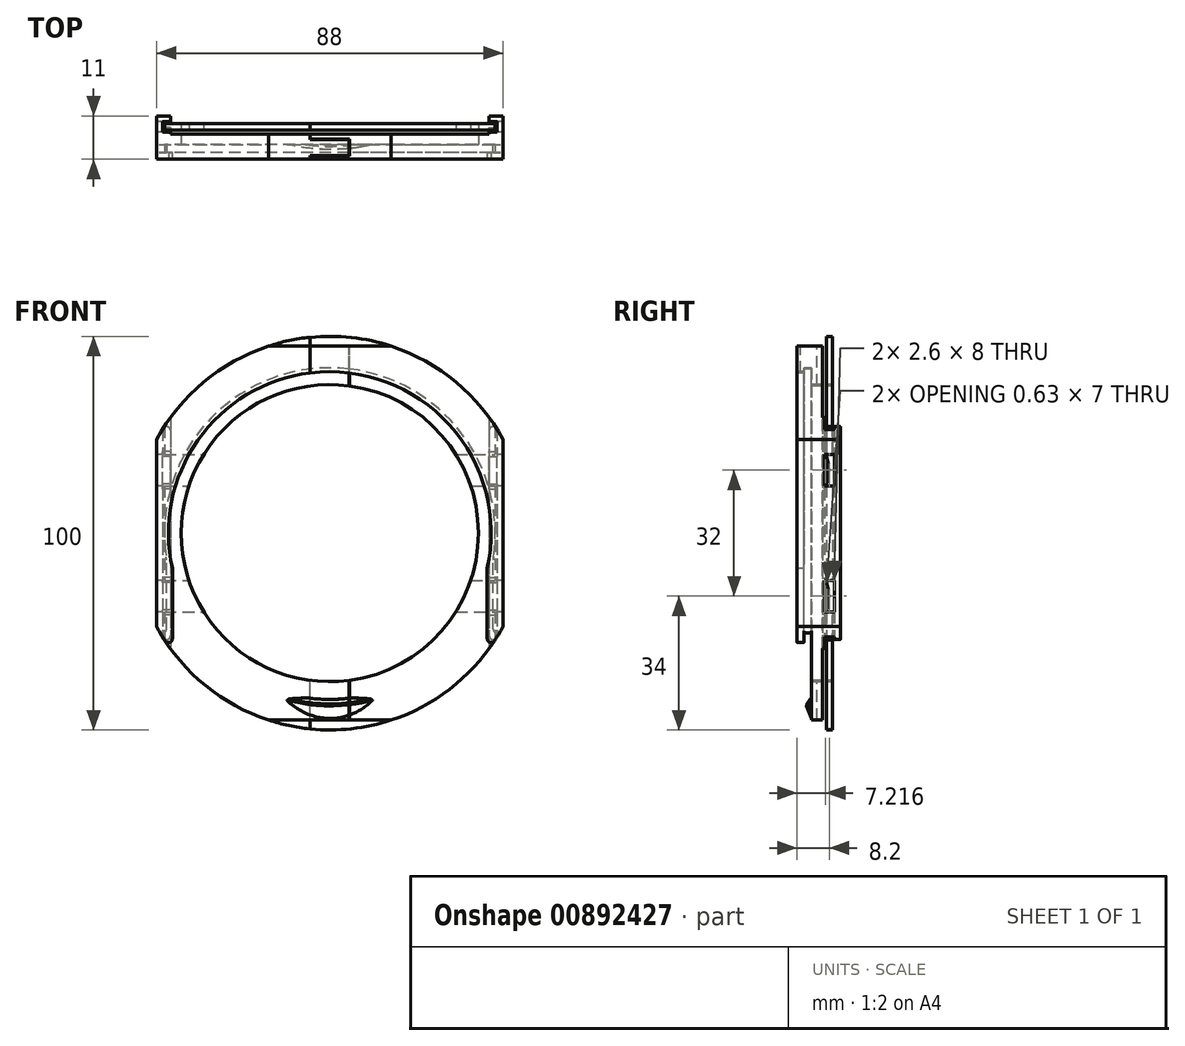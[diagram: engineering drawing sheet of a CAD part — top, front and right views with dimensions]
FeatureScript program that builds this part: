
annotation { "Feature Type Name" : "Feature", "Feature Type Description" : "" }
export const myFeature = defineFeature(function(context is Context, id is Id, definition is map)
    precondition{}
    {
        {
            var Q0;
            Q0=qCreatedBy(makeId("Front.planeOp"),FACE);
            var sketch = newSketch(context, id + "F0", { "sketchPlane" : qUnion([Q0])});
            skLineSegment(sketch, "E0.bottom", {"start": v(42, 50) * mm, "end": v(-42, 50) * mm});
            skLineSegment(sketch, "E0.top", {"start": v(42, -50) * mm, "end": v(-42, -50) * mm});
            skLineSegment(sketch, "E0.left", {"start": v(42, 50) * mm, "end": v(42, -50) * mm});
            skLineSegment(sketch, "E0.right", {"start": v(-42, 50) * mm, "end": v(-42, -50) * mm});
            skPoint(sketch, "E0.middle", {"position": v(0, 0) * mm});
            skSolve(sketch);
        }
        {
            var Q0;
            Q0=makeQuery(id+"F0.imprint","IMPRINT",FACE,{"disambiguationData":[TD([[makeQuery(id+"F0.imprint","IMPRINT",EDGE,{"derivedFrom":sQuery(id+"F0.wireOp",EDGE,"E0.bottom")}),1.0]])]});
            extrude(context, id + "F1", {"entities" : qUnion([Q0]), "depth" : .8 * mm, "offsetDistance" : 25 * mm, "hasSecondDirection" : true, "secondDirectionOppositeDirection" : true, "secondDirectionDepth" : .8 * mm});
        }
        {
            var Q0;
            Q0=qCreatedBy(makeId("Top.planeOp"),FACE);
            var sketch = newSketch(context, id + "F2", { "sketchPlane" : qUnion([Q0])});
            skLineSegment(sketch, "E1.0", {"start": v(42, 0.8) * mm, "end": v(-42, 0.8) * mm, "construction": true});
            skLineSegment(sketch, "E2.0", {"start": v(-42, -0.8) * mm, "end": v(-42, 0.8) * mm, "construction": true});
            skLineSegment(sketch, "E3.0", {"start": v(42, -0.8) * mm, "end": v(-42, -0.8) * mm, "construction": true});
            skLineSegment(sketch, "E4.0", {"start": v(42, -0.8) * mm, "end": v(42, 0.8) * mm, "construction": true});
            skLineSegment(sketch, "E5", {"start": v(-42.5, 1.3) * mm, "end": v(-42.5, -1.3) * mm});
            skLineSegment(sketch, "E6", {"start": v(-42.5, 1.3) * mm, "end": v(-40.5, 1.3) * mm});
            skLineSegment(sketch, "E7.MirrorCS", {"start": v(42.5, 1.3) * mm, "end": v(42.5, -1.3) * mm});
            skLineSegment(sketch, "E8.MirrorCS", {"start": v(42.5, 1.3) * mm, "end": v(40.5, 1.3) * mm});
            skLineSegment(sketch, "E9", {"start": v(-40.5, 1.3) * mm, "end": v(-40.5, 2.8) * mm});
            skLineSegment(sketch, "E10", {"start": v(-40.5, 2.8) * mm, "end": v(-44, 2.8) * mm});
            skLineSegment(sketch, "E11", {"start": v(-44, 2.8) * mm, "end": v(-44, -8.2) * mm});
            skLineSegment(sketch, "E12.MirrorCS", {"start": v(40.5, 1.3) * mm, "end": v(40.5, 2.8) * mm});
            skLineSegment(sketch, "E13.MirrorCS", {"start": v(40.5, 2.8) * mm, "end": v(44, 2.8) * mm});
            skLineSegment(sketch, "E14.MirrorCS", {"start": v(44, 2.8) * mm, "end": v(44, -8.2) * mm});
            skLineSegment(sketch, "E15", {"start": v(-44, -8.2) * mm, "end": v(44, -8.2) * mm});
            skLineSegment(sketch, "E16", {"start": v(-42.5, -1.3) * mm, "end": v(-40.5, -1.3) * mm});
            skLineSegment(sketch, "E17", {"start": v(-40.5, -1.3) * mm, "end": v(-40.5, -1.8) * mm});
            skLineSegment(sketch, "E18.MirrorCS", {"start": v(42.5, -1.3) * mm, "end": v(40.5, -1.3) * mm});
            skLineSegment(sketch, "E19.MirrorCS", {"start": v(40.5, -1.3) * mm, "end": v(40.5, -1.8) * mm});
            skLineSegment(sketch, "E20", {"start": v(40.5, -1.8) * mm, "end": v(-40.5, -1.8) * mm});
            skSolve(sketch);
        }
        {
            var Q0;
            Q0 = qSketchRegion(id + "F2", true);
            extrude(context, id + "F3", {"entities" : qUnion([Q0]), "endBound" : BoundingType.SYMMETRIC, "depth" : 95 * mm, "offsetDistance" : 25 * mm});
        }
        {
            var Q0;
            Q0=qCreatedBy(makeId("Right.planeOp"),FACE);
            var sketch = newSketch(context, id + "F4", { "sketchPlane" : qUnion([Q0])});
            skLineSegment(sketch, "E21.top", {"start": v(3, 37.75) * mm, "end": v(-4.5, 37.75) * mm});
            skLineSegment(sketch, "E22", {"start": v(-4.5, 37.75) * mm, "end": v(-4.5, 42) * mm});
            skLineSegment(sketch, "E23", {"start": v(-4.5, 42) * mm, "end": v(-6.5, 42) * mm});
            skLineSegment(sketch, "E24", {"start": v(-6.5, 42) * mm, "end": v(-6.5, 41) * mm});
            skLineSegment(sketch, "E25", {"start": v(-6.5, 41) * mm, "end": v(-8.5, 41) * mm});
            skLineSegment(sketch, "E26", {"start": v(-8.5, 41) * mm, "end": v(-8.5, 0) * mm});
            skLineSegment(sketch, "E27", {"start": v(3, 37.75) * mm, "end": v(3, 0) * mm});
            skLineSegment(sketch, "E28", {"start": v(3, 0) * mm, "end": v(-8.5, 0) * mm});
            skSolve(sketch);
        }
        {
            var Q0;
            Q0 = qSketchRegion(id + "F4", true);
            var Q1;
            Q1=sQuery(id+"F4.wireOp",EDGE,"E28");
            revolve(context, id + "F5", {"operationType" : NewBodyOperationType.REMOVE, "surfaceOperationType" : NewSurfaceOperationType.NEW, "entities" : qUnion([Q0]), "axis" : qUnion([Q1]), "revolveType" : RevolveType.FULL, "oppositeDirection" : true});
        }
        {
            var Q0;
            Q0=makeQuery(id+"F3.opExtrude","SWEPT_FACE",FACE,{"disambiguationData":[OSD([sQuery(id+"F2.wireOp",EDGE,"E15")])]});
            var sketch = newSketch(context, id + "F6", { "sketchPlane" : qUnion([Q0])});
            skLineSegment(sketch, "E29.0.0", {"start": v(-44, -47.5) * mm, "end": v(44, -47.5) * mm, "construction": true});
            skLineSegment(sketch, "E29.0.1", {"start": v(44, -47.5) * mm, "end": v(44, 47.5) * mm, "construction": true});
            skLineSegment(sketch, "E29.0.2", {"start": v(44, 47.5) * mm, "end": v(-44, 47.5) * mm, "construction": true});
            skLineSegment(sketch, "E29.0.3", {"start": v(-44, 47.5) * mm, "end": v(-44, -47.5) * mm, "construction": true});
            skLineSegment(sketch, "E30", {"start": v(-40, -9) * mm, "end": v(-40, -47.5) * mm});
            skLineSegment(sketch, "E31", {"start": v(40, -9) * mm, "end": v(40, -47.5) * mm});
            skArc(sketch, "E32", {"start": v(-40, -9) * mm, "mid": v(0, -41) * mm, "end": v(40, -9) * mm});
            skLineSegment(sketch, "E33", {"start": v(-40, -47.5) * mm, "end": v(40, -47.5) * mm});
            skSolve(sketch);
        }
        {
            var Q0;
            Q0 = qSketchRegion(id + "F6", true);
            var Q1;
            Q1=makeQuery(id+"F5.boolean.opBoolean","COPY",FACE,{"derivedFrom":makeQuery(id+"F5.opRevolve","SWEPT_FACE",FACE,{"disambiguationData":[OSD([sQuery(id+"F4.wireOp",EDGE,"E22")])]})});
            extrude(context, id + "F7", {"entities" : qUnion([Q0]), "operationType" : NewBodyOperationType.REMOVE, "endBound" : BoundingType.UP_TO_SURFACE, "oppositeDirection" : true, "depth" : 25 * mm, "endBoundEntityFace" : qUnion([Q1]), "offsetDistance" : 25 * mm});
        }
        {
            var Q0;
            Q0=qCreatedBy(makeId("Front.planeOp"),FACE);
            var sketch = newSketch(context, id + "F8", { "sketchPlane" : qUnion([Q0])});
            skCircle(sketch, "E34", {"center": v(0, 0) * mm, "radius": 50 * mm});
            skCircle(sketch, "E35", {"center": v(0, 0) * mm, "radius": 70 * mm});
            skSolve(sketch);
        }
        {
            var Q0;
            Q0 = qSketchRegion(id + "F8", true);
            extrude(context, id + "F9", {"entities" : qUnion([Q0]), "operationType" : NewBodyOperationType.REMOVE, "endBound" : BoundingType.SYMMETRIC, "oppositeDirection" : true, "depth" : 500 * mm, "offsetDistance" : 25 * mm});
        }
        {
            var Q0;
            Q0=qCreatedBy(makeId("Top.planeOp"),FACE);
            var sketch = newSketch(context, id + "F10", { "sketchPlane" : qUnion([Q0])});
            skLineSegment(sketch, "E36", {"start": v(-42, -4.5) * mm, "end": v(-42, -3.5) * mm, "construction": true});
            skLineSegment(sketch, "E37", {"start": v(42, -4.5) * mm, "end": v(42, -6.5) * mm, "construction": true});
            skLineSegment(sketch, "E38.bottom", {"start": v(-41.5, -4.5) * mm, "end": v(41.5, -4.5) * mm});
            skLineSegment(sketch, "E38.left", {"start": v(-41.5, -6.5) * mm, "end": v(-41.5, -4.5) * mm});
            skLineSegment(sketch, "E38.right", {"start": v(41.5, -6.5) * mm, "end": v(41.5, -4.5) * mm});
            skLineSegment(sketch, "E39.0.0", {"start": v(-15.61, -4.5) * mm, "end": v(15.61, -4.5) * mm});
            skLineSegment(sketch, "E39.0.1", {"start": v(15.61, -4.5) * mm, "end": v(40, -4.5) * mm});
            skLineSegment(sketch, "E39.0.3", {"start": v(42, -4.5) * mm, "end": v(-42, -4.5) * mm, "construction": true});
            skLineSegment(sketch, "E39.0.5", {"start": v(-40, -4.5) * mm, "end": v(-15.61, -4.5) * mm});
            skLineSegment(sketch, "E40.0", {"start": v(41, -6.5) * mm, "end": v(-41, -6.5) * mm, "construction": true});
            skLineSegment(sketch, "E41", {"start": v(-41.5, -6.5) * mm, "end": v(41.5, -6.5) * mm});
            skSolve(sketch);
        }
        {
            var Q0;
            Q0 = qSketchRegion(id + "F10", true);
            extrude(context, id + "F11", {"entities" : qUnion([Q0]), "operationType" : NewBodyOperationType.REMOVE, "oppositeDirection" : true, "depth" : 50 * mm, "offsetDistance" : 25 * mm});
        }
        {
            var Q0;
            Q0=makeQuery(id+"F11.boolean.opBoolean","INTERSECT",EDGE,{"derivedFrom":[makeQuery(id+"F5.boolean.opBoolean","COPY",FACE,{"derivedFrom":makeQuery(id+"F5.opRevolve","SWEPT_FACE",FACE,{"disambiguationData":[OSD([sQuery(id+"F4.wireOp",EDGE,"E23")])]})}),makeQuery(id+"F11.opExtrude","SWEPT_FACE",FACE,{"disambiguationData":[OSD([sQuery(id+"F10.wireOp",EDGE,"E38.right")])]})]});
            var Q1;
            Q1=makeQuery(id+"F11.boolean.opBoolean","INTERSECT",EDGE,{"derivedFrom":[makeQuery(id+"F5.boolean.opBoolean","COPY",FACE,{"derivedFrom":makeQuery(id+"F5.opRevolve","SWEPT_FACE",FACE,{"disambiguationData":[OSD([sQuery(id+"F4.wireOp",EDGE,"E23")])]})}),makeQuery(id+"F11.opExtrude","SWEPT_FACE",FACE,{"disambiguationData":[OSD([sQuery(id+"F10.wireOp",EDGE,"E38.left")])]})]});
            fillet(context, id + "F12", {"entities" : qUnion([Q0, Q1]), "radius" : 5 * mm, "tangentPropagation" : true, "allowEdgeOverflow" : false});
        }
        {
            var Q0;
            {var subQ0=sQuery(id+"F2.wireOp",EDGE,"E16");var subQ1=sQuery(id+"F2.wireOp",EDGE,"E11");var subQ2=sQuery(id+"F2.wireOp",EDGE,"E10");var subQ3=sQuery(id+"F2.wireOp",EDGE,"E5");var subQ4=sQuery(id+"F2.wireOp",EDGE,"E15");var subQ5=sQuery(id+"F2.wireOp",EDGE,"E20");var subQ6=sQuery(id+"F2.wireOp",EDGE,"E17");var subQ7=sQuery(id+"F2.wireOp",EDGE,"E9");var subQ8=sQuery(id+"F2.wireOp",EDGE,"E6");Q0=makeQuery(id+"F11.boolean.opBoolean","INTERSECT",EDGE,{"derivedFrom":[makeQuery(id+"F9.boolean.opBoolean","COPY",FACE,{"disambiguationData":[TD([makeQuery(id+"F3.opExtrude","SWEPT_FACE",FACE,{"disambiguationData":[OSD([subQ3])]}),makeQuery(id+"F3.opExtrude","CAP_FACE",FACE,{"disambiguationData":[OSD([subQ3,subQ8,sQuery(id+"F2.wireOp",EDGE,"E7.MirrorCS"),sQuery(id+"F2.wireOp",EDGE,"E8.MirrorCS"),subQ7,subQ2,subQ1,sQuery(id+"F2.wireOp",EDGE,"E12.MirrorCS"),sQuery(id+"F2.wireOp",EDGE,"E13.MirrorCS"),sQuery(id+"F2.wireOp",EDGE,"E14.MirrorCS"),subQ4,subQ0,subQ6,sQuery(id+"F2.wireOp",EDGE,"E18.MirrorCS"),sQuery(id+"F2.wireOp",EDGE,"E19.MirrorCS"),subQ5])],"isStart":true}),makeQuery(id+"F3.opExtrude","SWEPT_FACE",FACE,{"disambiguationData":[OSD([subQ8])]}),makeQuery(id+"F3.opExtrude","SWEPT_FACE",FACE,{"disambiguationData":[OSD([subQ7])]}),makeQuery(id+"F3.opExtrude","SWEPT_FACE",FACE,{"disambiguationData":[OSD([subQ2])]}),makeQuery(id+"F3.opExtrude","SWEPT_FACE",FACE,{"disambiguationData":[OSD([subQ1])]}),makeQuery(id+"F3.opExtrude","SWEPT_FACE",FACE,{"disambiguationData":[OSD([subQ4])]}),makeQuery(id+"F3.opExtrude","SWEPT_FACE",FACE,{"disambiguationData":[OSD([subQ0])]}),makeQuery(id+"F3.opExtrude","SWEPT_FACE",FACE,{"disambiguationData":[OSD([subQ6])]}),makeQuery(id+"F3.opExtrude","SWEPT_FACE",FACE,{"disambiguationData":[OSD([subQ5])]}),makeQuery(id+"F5.boolean.opBoolean","COPY",FACE,{"derivedFrom":makeQuery(id+"F5.opRevolve","SWEPT_FACE",FACE,{"disambiguationData":[OSD([sQuery(id+"F4.wireOp",EDGE,"t31NqOFZ-bdFC-osZE-Ytuw-QL428Am0EnsE")])]})}),makeQuery(id+"F7.boolean.opBoolean","COPY",FACE,{"derivedFrom":makeQuery(id+"F7.opExtrude","SWEPT_FACE",FACE,{"disambiguationData":[OSD([sQuery(id+"F6.wireOp",EDGE,"E30")])]})})])],"derivedFrom":makeQuery(id+"F9.opExtrude","SWEPT_FACE",FACE,{"disambiguationData":[OSD([sQuery(id+"F8.wireOp",EDGE,"E34")])]})}),makeQuery(id+"F11.opExtrude","SWEPT_FACE",FACE,{"disambiguationData":[OSD([sQuery(id+"F10.wireOp",EDGE,"E38.left")])]})]});}
            var Q1;
            {var subQ0=sQuery(id+"F2.wireOp",EDGE,"E20");var subQ1=sQuery(id+"F2.wireOp",EDGE,"E14.MirrorCS");var subQ2=sQuery(id+"F2.wireOp",EDGE,"E13.MirrorCS");var subQ3=sQuery(id+"F2.wireOp",EDGE,"E15");var subQ4=sQuery(id+"F2.wireOp",EDGE,"E19.MirrorCS");var subQ5=sQuery(id+"F2.wireOp",EDGE,"E18.MirrorCS");var subQ6=sQuery(id+"F2.wireOp",EDGE,"E12.MirrorCS");var subQ7=sQuery(id+"F2.wireOp",EDGE,"E8.MirrorCS");var subQ8=sQuery(id+"F2.wireOp",EDGE,"E7.MirrorCS");Q1=makeQuery(id+"F11.boolean.opBoolean","INTERSECT",EDGE,{"derivedFrom":[makeQuery(id+"F9.boolean.opBoolean","COPY",FACE,{"disambiguationData":[TD([makeQuery(id+"F3.opExtrude","CAP_FACE",FACE,{"disambiguationData":[OSD([sQuery(id+"F2.wireOp",EDGE,"E5"),sQuery(id+"F2.wireOp",EDGE,"E6"),subQ8,subQ7,sQuery(id+"F2.wireOp",EDGE,"E9"),sQuery(id+"F2.wireOp",EDGE,"E10"),sQuery(id+"F2.wireOp",EDGE,"E11"),subQ6,subQ2,subQ1,subQ3,sQuery(id+"F2.wireOp",EDGE,"E16"),sQuery(id+"F2.wireOp",EDGE,"E17"),subQ5,subQ4,subQ0])],"isStart":true}),makeQuery(id+"F3.opExtrude","SWEPT_FACE",FACE,{"disambiguationData":[OSD([subQ8])]}),makeQuery(id+"F3.opExtrude","SWEPT_FACE",FACE,{"disambiguationData":[OSD([subQ7])]}),makeQuery(id+"F3.opExtrude","SWEPT_FACE",FACE,{"disambiguationData":[OSD([subQ6])]}),makeQuery(id+"F3.opExtrude","SWEPT_FACE",FACE,{"disambiguationData":[OSD([subQ2])]}),makeQuery(id+"F3.opExtrude","SWEPT_FACE",FACE,{"disambiguationData":[OSD([subQ1])]}),makeQuery(id+"F3.opExtrude","SWEPT_FACE",FACE,{"disambiguationData":[OSD([subQ3])]}),makeQuery(id+"F3.opExtrude","SWEPT_FACE",FACE,{"disambiguationData":[OSD([subQ5])]}),makeQuery(id+"F3.opExtrude","SWEPT_FACE",FACE,{"disambiguationData":[OSD([subQ4])]}),makeQuery(id+"F3.opExtrude","SWEPT_FACE",FACE,{"disambiguationData":[OSD([subQ0])]}),makeQuery(id+"F5.boolean.opBoolean","COPY",FACE,{"derivedFrom":makeQuery(id+"F5.opRevolve","SWEPT_FACE",FACE,{"disambiguationData":[OSD([sQuery(id+"F4.wireOp",EDGE,"t31NqOFZ-bdFC-osZE-Ytuw-QL428Am0EnsE")])]})}),makeQuery(id+"F7.boolean.opBoolean","COPY",FACE,{"derivedFrom":makeQuery(id+"F7.opExtrude","SWEPT_FACE",FACE,{"disambiguationData":[OSD([sQuery(id+"F6.wireOp",EDGE,"E31")])]})})])],"derivedFrom":makeQuery(id+"F9.opExtrude","SWEPT_FACE",FACE,{"disambiguationData":[OSD([sQuery(id+"F8.wireOp",EDGE,"E34")])]})}),makeQuery(id+"F11.opExtrude","SWEPT_FACE",FACE,{"disambiguationData":[OSD([sQuery(id+"F10.wireOp",EDGE,"E38.right")])]})]});}
            fillet(context, id + "F13", {"entities" : qUnion([Q0, Q1]), "radius" : 1 * mm, "tangentPropagation" : true, "allowEdgeOverflow" : false});
        }
        {
            var Q0;
            Q0=qCreatedBy(makeId("Right.planeOp"),FACE);
            var sketch = newSketch(context, id + "F14", { "sketchPlane" : qUnion([Q0])});
            skLineSegment(sketch, "E42.0.0", {"start": v(-8.2, 23.75) * mm, "end": v(2.8, 23.75) * mm, "construction": true});
            skLineSegment(sketch, "E42.0.1", {"start": v(2.8, 23.75) * mm, "end": v(2.8, -23.75) * mm, "construction": true});
            skLineSegment(sketch, "E42.0.2", {"start": v(-8.2, -23.75) * mm, "end": v(2.8, -23.75) * mm, "construction": true});
            skLineSegment(sketch, "E42.0.3", {"start": v(-8.2, -23.75) * mm, "end": v(-8.2, 23.75) * mm, "construction": true});
            skLineSegment(sketch, "E43.0", {"start": v(1.3, 26.34) * mm, "end": v(-1.3, 26.34) * mm, "construction": true});
            skLineSegment(sketch, "E44.0", {"start": v(-1.3, -26.34) * mm, "end": v(1.3, -26.34) * mm, "construction": true});
            skLineSegment(sketch, "E45.bottom", {"start": v(1.3, 20) * mm, "end": v(-1.3, 20) * mm});
            skLineSegment(sketch, "E45.top", {"start": v(1.3, 12) * mm, "end": v(-1.3, 12) * mm});
            skLineSegment(sketch, "E45.left", {"start": v(1.3, 20) * mm, "end": v(1.3, 12) * mm});
            skLineSegment(sketch, "E45.right", {"start": v(-1.3, 20) * mm, "end": v(-1.3, 12) * mm});
            skLineSegment(sketch, "E46.MirrorCS", {"start": v(1.3, -20) * mm, "end": v(-1.3, -20) * mm});
            skLineSegment(sketch, "E47.MirrorCS", {"start": v(-1.3, -20) * mm, "end": v(-1.3, -12) * mm});
            skLineSegment(sketch, "E48.MirrorCS", {"start": v(1.3, -12) * mm, "end": v(-1.3, -12) * mm});
            skLineSegment(sketch, "E49.MirrorCS", {"start": v(1.3, -20) * mm, "end": v(1.3, -12) * mm});
            skSolve(sketch);
        }
        {
            var Q0;
            Q0=makeQuery(id+"F14.imprint","IMPRINT",FACE,{"disambiguationData":[TD([[makeQuery(id+"F14.imprint","IMPRINT",EDGE,{"derivedFrom":sQuery(id+"F14.wireOp",EDGE,"E45.bottom")}),1.0]])]});
            var Q1;
            Q1=makeQuery(id+"F14.imprint","IMPRINT",FACE,{"disambiguationData":[TD([[makeQuery(id+"F14.imprint","IMPRINT",EDGE,{"derivedFrom":sQuery(id+"F14.wireOp",EDGE,"E46.MirrorCS")}),-1.0]])]});
            extrude(context, id + "F15", {"entities" : qUnion([Q0, Q1]), "operationType" : NewBodyOperationType.REMOVE, "endBound" : BoundingType.SYMMETRIC, "depth" : 100 * mm, "offsetDistance" : 25 * mm});
        }
        {
            var Q0;
            Q0=makeQuery(id+"F15.boolean.opBoolean","SPLIT",FACE,{"disambiguationData":[TD([makeQuery(id+"F15.opExtrude","SWEPT_FACE",FACE,{"disambiguationData":[OSD([sQuery(id+"F14.wireOp",EDGE,"E45.top")])]})])],"derivedFrom":makeQuery(id+"F3.opExtrude","SWEPT_FACE",FACE,{"disambiguationData":[OSD([sQuery(id+"F2.wireOp",EDGE,"E5")])]})});
            var sketch = newSketch(context, id + "F16", { "sketchPlane" : qUnion([Q0])});
            skLineSegment(sketch, "E50.0", {"start": v(-1.3, 20) * mm, "end": v(1.3, 20) * mm, "construction": true});
            skLineSegment(sketch, "E51.0", {"start": v(-1.3, 12) * mm, "end": v(1.3, 12) * mm, "construction": true});
            skArc(sketch, "E52", {"start": v(-1.3, 12.5) * mm, "mid": v(-0.67, 16) * mm, "end": v(-1.3, 19.5) * mm});
            skLineSegment(sketch, "E53", {"start": v(6.42, 16) * mm, "end": v(-9.93, 16) * mm, "construction": true});
            skArc(sketch, "E54.0", {"start": v(-1.3, 11.26) * mm, "mid": v(-0.17, 16) * mm, "end": v(-1.3, 20.74) * mm});
            skLineSegment(sketch, "E55", {"start": v(-1.3, 20.74) * mm, "end": v(-1.3, 19.5) * mm});
            skLineSegment(sketch, "E56", {"start": v(-1.3, 12.5) * mm, "end": v(-1.3, 11.26) * mm});
            skSolve(sketch);
        }
        {
            var Q0;
            {var subQ0=sQuery(id+"F16.wireOp",EDGE,"E55");Q0=makeQuery(id+"F16.imprint","IMPRINT",FACE,{"disambiguationData":[TD([[makeQuery(id+"F16.imprint","IMPRINT",EDGE,{"derivedFrom":subQ0}),1.0]])]});}
            var Q1;
            {var subQ0=sQuery(id+"F16.wireOp",EDGE,"E56");Q1=makeQuery(id+"F16.imprint","IMPRINT",FACE,{"disambiguationData":[TD([[makeQuery(id+"F16.imprint","IMPRINT",EDGE,{"derivedFrom":subQ0}),1.0]])]});}
            extrude(context, id + "F17", {"entities" : qUnion([Q0, Q1]), "depth" : 2 * mm, "offsetDistance" : 25 * mm});
        }
        {
            var Q0;
            Q0=makeQuery(id+"F17.opExtrude","SWEPT_BODY",BODY,{"disambiguationData":[OSD([sQuery(id+"F16.wireOp",EDGE,"E52"),sQuery(id+"F16.wireOp",EDGE,"E54.0"),sQuery(id+"F16.wireOp",EDGE,"E55"),sQuery(id+"F16.wireOp",EDGE,"E56")])]});
            var Q1;
            Q1=qCreatedBy(makeId("Right.planeOp"),FACE);
            mirror(context, id + "F18", {"entities" : qUnion([Q0]), "mirrorPlane" : qUnion([Q1])});
        }
        {
            var Q0;
            Q0=makeQuery(id+"F18.opPattern","COPY",BODY,{"derivedFrom":makeQuery(id+"F17.opExtrude","SWEPT_BODY",BODY,{"disambiguationData":[OSD([sQuery(id+"F16.wireOp",EDGE,"E52"),sQuery(id+"F16.wireOp",EDGE,"E54.0"),sQuery(id+"F16.wireOp",EDGE,"E55"),sQuery(id+"F16.wireOp",EDGE,"E56")])]}),"instanceName":"1"});
            var Q1;
            Q1=makeQuery(id+"F17.opExtrude","SWEPT_BODY",BODY,{"disambiguationData":[OSD([sQuery(id+"F16.wireOp",EDGE,"E52"),sQuery(id+"F16.wireOp",EDGE,"E54.0"),sQuery(id+"F16.wireOp",EDGE,"E55"),sQuery(id+"F16.wireOp",EDGE,"E56")])]});
            var Q2;
            Q2=qCreatedBy(makeId("Top.planeOp"),FACE);
            mirror(context, id + "F19", {"operationType" : NewBodyOperationType.ADD, "entities" : qUnion([Q0, Q1]), "mirrorPlane" : qUnion([Q2])});
        }
        {
            var Q0;
            Q0=makeQuery(id+"F9.boolean.opBoolean","INTERSECT",EDGE,{"derivedFrom":[makeQuery(id+"F7.boolean.opBoolean","COPY",FACE,{"derivedFrom":makeQuery(id+"F7.opExtrude","SWEPT_FACE",FACE,{"disambiguationData":[OSD([sQuery(id+"F6.wireOp",EDGE,"E31")])]})}),makeQuery(id+"F9.opExtrude","SWEPT_FACE",FACE,{"disambiguationData":[OSD([sQuery(id+"F8.wireOp",EDGE,"E34")])]})]});
            var Q1;
            Q1=makeQuery(id+"F9.boolean.opBoolean","INTERSECT",EDGE,{"derivedFrom":[makeQuery(id+"F7.boolean.opBoolean","COPY",FACE,{"derivedFrom":makeQuery(id+"F7.opExtrude","SWEPT_FACE",FACE,{"disambiguationData":[OSD([sQuery(id+"F6.wireOp",EDGE,"E30")])]})}),makeQuery(id+"F9.opExtrude","SWEPT_FACE",FACE,{"disambiguationData":[OSD([sQuery(id+"F8.wireOp",EDGE,"E34")])]})]});
            var Q2;
            Q2=makeQuery(id+"F9.boolean.opBoolean","INTERSECT",EDGE,{"disambiguationData":[OD(1.0)],"derivedFrom":[makeQuery(id+"F3.opExtrude","SWEPT_FACE",FACE,{"disambiguationData":[OSD([sQuery(id+"F2.wireOp",EDGE,"E12.MirrorCS")])]}),makeQuery(id+"F9.opExtrude","SWEPT_FACE",FACE,{"disambiguationData":[OSD([sQuery(id+"F8.wireOp",EDGE,"E34")])]})]});
            var Q3;
            Q3=makeQuery(id+"F9.boolean.opBoolean","INTERSECT",EDGE,{"disambiguationData":[OD(1.0)],"derivedFrom":[makeQuery(id+"F3.opExtrude","SWEPT_FACE",FACE,{"disambiguationData":[OSD([sQuery(id+"F2.wireOp",EDGE,"E9")])]}),makeQuery(id+"F9.opExtrude","SWEPT_FACE",FACE,{"disambiguationData":[OSD([sQuery(id+"F8.wireOp",EDGE,"E34")])]})]});
            var Q4;
            Q4=makeQuery(id+"F9.boolean.opBoolean","INTERSECT",EDGE,{"disambiguationData":[OD(0.0)],"derivedFrom":[makeQuery(id+"F3.opExtrude","SWEPT_FACE",FACE,{"disambiguationData":[OSD([sQuery(id+"F2.wireOp",EDGE,"E9")])]}),makeQuery(id+"F9.opExtrude","SWEPT_FACE",FACE,{"disambiguationData":[OSD([sQuery(id+"F8.wireOp",EDGE,"E34")])]})]});
            var Q5;
            Q5=makeQuery(id+"F9.boolean.opBoolean","INTERSECT",EDGE,{"disambiguationData":[OD(0.0)],"derivedFrom":[makeQuery(id+"F3.opExtrude","SWEPT_FACE",FACE,{"disambiguationData":[OSD([sQuery(id+"F2.wireOp",EDGE,"E12.MirrorCS")])]}),makeQuery(id+"F9.opExtrude","SWEPT_FACE",FACE,{"disambiguationData":[OSD([sQuery(id+"F8.wireOp",EDGE,"E34")])]})]});
            fillet(context, id + "F20", {"entities" : qUnion([Q0, Q1, Q2, Q3, Q4, Q5]), "radius" : 1 * mm, "tangentPropagation" : true, "allowEdgeOverflow" : false});
        }
        {
            var Q0;
            Q0=makeQuery(id+"F11.boolean.opBoolean","MERGE",FACE,{"derivedFrom":[makeQuery(id+"F7.boolean.opBoolean","MERGE",FACE,{"derivedFrom":[makeQuery(id+"F5.boolean.opBoolean","COPY",FACE,{"derivedFrom":makeQuery(id+"F5.opRevolve","SWEPT_FACE",FACE,{"disambiguationData":[OSD([sQuery(id+"F4.wireOp",EDGE,"E22")])]})})],"fromTools":[makeQuery(id+"F7.opExtrude","CAP_FACE",FACE,{"disambiguationData":[OSD([sQuery(id+"F6.wireOp",EDGE,"E30"),sQuery(id+"F6.wireOp",EDGE,"E31"),sQuery(id+"F6.wireOp",EDGE,"E32"),sQuery(id+"F6.wireOp",EDGE,"E33")])],"isStart":false})]})],"fromTools":[makeQuery(id+"F11.opExtrude","SWEPT_FACE",FACE,{"disambiguationData":[OSD([sQuery(id+"F10.wireOp",EDGE,"E38.bottom"),sQuery(id+"F10.wireOp",EDGE,"E39.0.0"),sQuery(id+"F10.wireOp",EDGE,"E39.0.1"),sQuery(id+"F10.wireOp",EDGE,"E39.0.5")])]})]});
            var sketch = newSketch(context, id + "F21", { "sketchPlane" : qUnion([Q0])});
            skArc(sketch, "E57", {"start": v(-12.5, -40.36) * mm, "mid": v(0, -42.25) * mm, "end": v(12.5, -40.36) * mm});
            skArc(sketch, "E58", {"start": v(-12.5, -40.36) * mm, "mid": v(0, -47.07) * mm, "end": v(12.5, -40.36) * mm});
            skSolve(sketch);
        }
        {
            var Q0;
            Q0=makeQuery(id+"F21.imprint","IMPRINT",FACE,{"disambiguationData":[TD([[makeQuery(id+"F21.imprint","IMPRINT",EDGE,{"derivedFrom":sQuery(id+"F21.wireOp",EDGE,"E57")}),-1.0]])]});
            extrude(context, id + "F22", {"entities" : qUnion([Q0]), "operationType" : NewBodyOperationType.ADD, "depth" : 2 * mm, "offsetDistance" : 25 * mm});
        }
        {
            var Q0;
            Q0=makeQuery(id+"F22.opExtrude","CAP_EDGE",EDGE,{"disambiguationData":[OSD([sQuery(id+"F21.wireOp",EDGE,"E58")])],"isStart":false});
            chamfer(context, id + "F23", {"entities" : qUnion([Q0]), "chamferType" : ChamferType.TWO_OFFSETS, "width1" : 5 * mm, "oppositeDirection" : false, "width2" : 2 * mm, "tangentPropagation" : true});
        }
        {
            var Q0;
            Q0=makeQuery(id+"F23.opChamfer","BLEND_EDGE",EDGE,{"blendedFrom":[makeQuery(id+"F22.opExtrude","CAP_EDGE",EDGE,{"disambiguationData":[OSD([sQuery(id+"F21.wireOp",EDGE,"E58")])],"isStart":false}),makeQuery(id+"F22.opExtrude","SWEPT_FACE",FACE,{"disambiguationData":[OSD([sQuery(id+"F21.wireOp",EDGE,"E57")])]})],"blendedInto":[makeQuery(id+"F22.opExtrude","SWEPT_FACE",FACE,{"disambiguationData":[OSD([sQuery(id+"F21.wireOp",EDGE,"E57")])]})]});
            chamfer(context, id + "F24", {"entities" : qUnion([Q0]), "width" : 1 * mm, "tangentPropagation" : true});
        }
        {
            var Q0;
            {var subQ0=sQuery(id+"F21.wireOp",EDGE,"E58");Q0=makeQuery(id+"F24.opChamfer","BLEND_EDGE",EDGE,{"blendedFrom":[makeQuery(id+"F23.opChamfer","BLEND_EDGE",EDGE,{"blendedFrom":[makeQuery(id+"F22.opExtrude","CAP_EDGE",EDGE,{"disambiguationData":[OSD([subQ0])],"isStart":false}),makeQuery(id+"F22.opExtrude","SWEPT_FACE",FACE,{"disambiguationData":[OSD([sQuery(id+"F21.wireOp",EDGE,"E57")])]})],"blendedInto":[makeQuery(id+"F22.opExtrude","SWEPT_FACE",FACE,{"disambiguationData":[OSD([sQuery(id+"F21.wireOp",EDGE,"E57")])]})]}),makeQuery(id+"F23.opChamfer","BLEND_FACE",FACE,{"disambiguationData":[OSD([subQ0])]})],"blendedInto":[makeQuery(id+"F23.opChamfer","BLEND_FACE",FACE,{"disambiguationData":[OSD([subQ0])]})]});}
            chamfer(context, id + "F25", {"entities" : qUnion([Q0]), "width" : .5 * mm, "tangentPropagation" : true});
        }
        {
            var Q0;
            Q0=qCreatedBy(makeId("Top.planeOp"),FACE);
            var sketch = newSketch(context, id + "F26", { "sketchPlane" : qUnion([Q0])});
            skLineSegment(sketch, "E59", {"start": v(0, -27) * mm, "end": v(-59.98, 15) * mm});
            skLineSegment(sketch, "E60", {"start": v(-59.98, 15) * mm, "end": v(0, 15) * mm});
            skLineSegment(sketch, "E61", {"start": v(0, 15) * mm, "end": v(0, -27) * mm});
            skSolve(sketch);
        }
        {
            var Q0;
            Q0=qCreatedBy(makeId("Top.planeOp"),FACE);
            var sketch = newSketch(context, id + "F27", { "sketchPlane" : qUnion([Q0])});
            skLineSegment(sketch, "E62", {"start": v(-5, -18.8) * mm, "end": v(-5, -7.35) * mm, "construction": true});
            skLineSegment(sketch, "E63", {"start": v(-5, -7.35) * mm, "end": v(5, -7.35) * mm, "construction": true});
            skLineSegment(sketch, "E64", {"start": v(5, -7.35) * mm, "end": v(5, -3.15) * mm, "construction": true});
            skLineSegment(sketch, "E65", {"start": v(5, -3.15) * mm, "end": v(-5, -3.15) * mm, "construction": true});
            skLineSegment(sketch, "E66", {"start": v(-5, -3.15) * mm, "end": v(-5, 8.08) * mm, "construction": true});
            skLineSegment(sketch, "E67.0", {"start": v(41, -8.2) * mm, "end": v(-41, -8.2) * mm, "construction": true});
            skLineSegment(sketch, "E68.0", {"start": v(41, -6.5) * mm, "end": v(-41, -6.5) * mm, "construction": true});
            skLineSegment(sketch, "E69.0", {"start": v(15.61, -1.8) * mm, "end": v(-15.61, -1.8) * mm, "construction": true});
            skLineSegment(sketch, "E70.0", {"start": v(-4.95, -3.1) * mm, "end": v(-4.95, 8.08) * mm});
            skLineSegment(sketch, "E70.1", {"start": v(-4.95, -18.8) * mm, "end": v(-4.95, -7.4) * mm});
            skLineSegment(sketch, "E70.2", {"start": v(-4.95, -7.4) * mm, "end": v(5.05, -7.4) * mm});
            skLineSegment(sketch, "E70.3", {"start": v(5.05, -7.4) * mm, "end": v(5.05, -3.1) * mm});
            skLineSegment(sketch, "E70.4", {"start": v(5.05, -3.1) * mm, "end": v(-4.95, -3.1) * mm});
            skLineSegment(sketch, "E71.0", {"start": v(-5.05, -3.2) * mm, "end": v(-5.05, 8.08) * mm});
            skLineSegment(sketch, "E72.0", {"start": v(4.95, -3.2) * mm, "end": v(-5.05, -3.2) * mm});
            skLineSegment(sketch, "E73.0", {"start": v(4.95, -7.3) * mm, "end": v(4.95, -3.2) * mm});
            skLineSegment(sketch, "E74.0", {"start": v(-5.05, -7.3) * mm, "end": v(4.95, -7.3) * mm});
            skLineSegment(sketch, "E75.0", {"start": v(-5.05, -18.8) * mm, "end": v(-5.05, -7.3) * mm});
            skLineSegment(sketch, "E76", {"start": v(-5.05, 8.08) * mm, "end": v(-4.95, 8.08) * mm});
            skLineSegment(sketch, "E77", {"start": v(-5.05, -18.8) * mm, "end": v(-4.95, -18.8) * mm});
            skLineSegment(sketch, "E78.0.3", {"start": v(41.5, -4.5) * mm, "end": v(41.55, -4.5) * mm});
            skLineSegment(sketch, "E78.0.4", {"start": v(42, -4.5) * mm, "end": v(-42, -4.5) * mm, "construction": true});
            skLineSegment(sketch, "E78.0.5", {"start": v(-41.55, -4.5) * mm, "end": v(-41.5, -4.5) * mm});
            skLineSegment(sketch, "E78.0.7", {"start": v(-41.5, -4.5) * mm, "end": v(-43.37, -4.5) * mm});
            skSolve(sketch);
        }
        {
            var Q0;
            Q0=makeQuery(id+"F27.imprint","IMPRINT",FACE,{"disambiguationData":[TD([[makeQuery(id+"F27.imprint","IMPRINT",EDGE,{"derivedFrom":sQuery(id+"F27.wireOp",EDGE,"E70.0")}),1.0]])]});
            extrude(context, id + "F28", {"entities" : qUnion([Q0]), "operationType" : NewBodyOperationType.REMOVE, "endBound" : BoundingType.SYMMETRIC, "oppositeDirection" : true, "depth" : 500 * mm, "offsetDistance" : 25 * mm});
        }
    });
